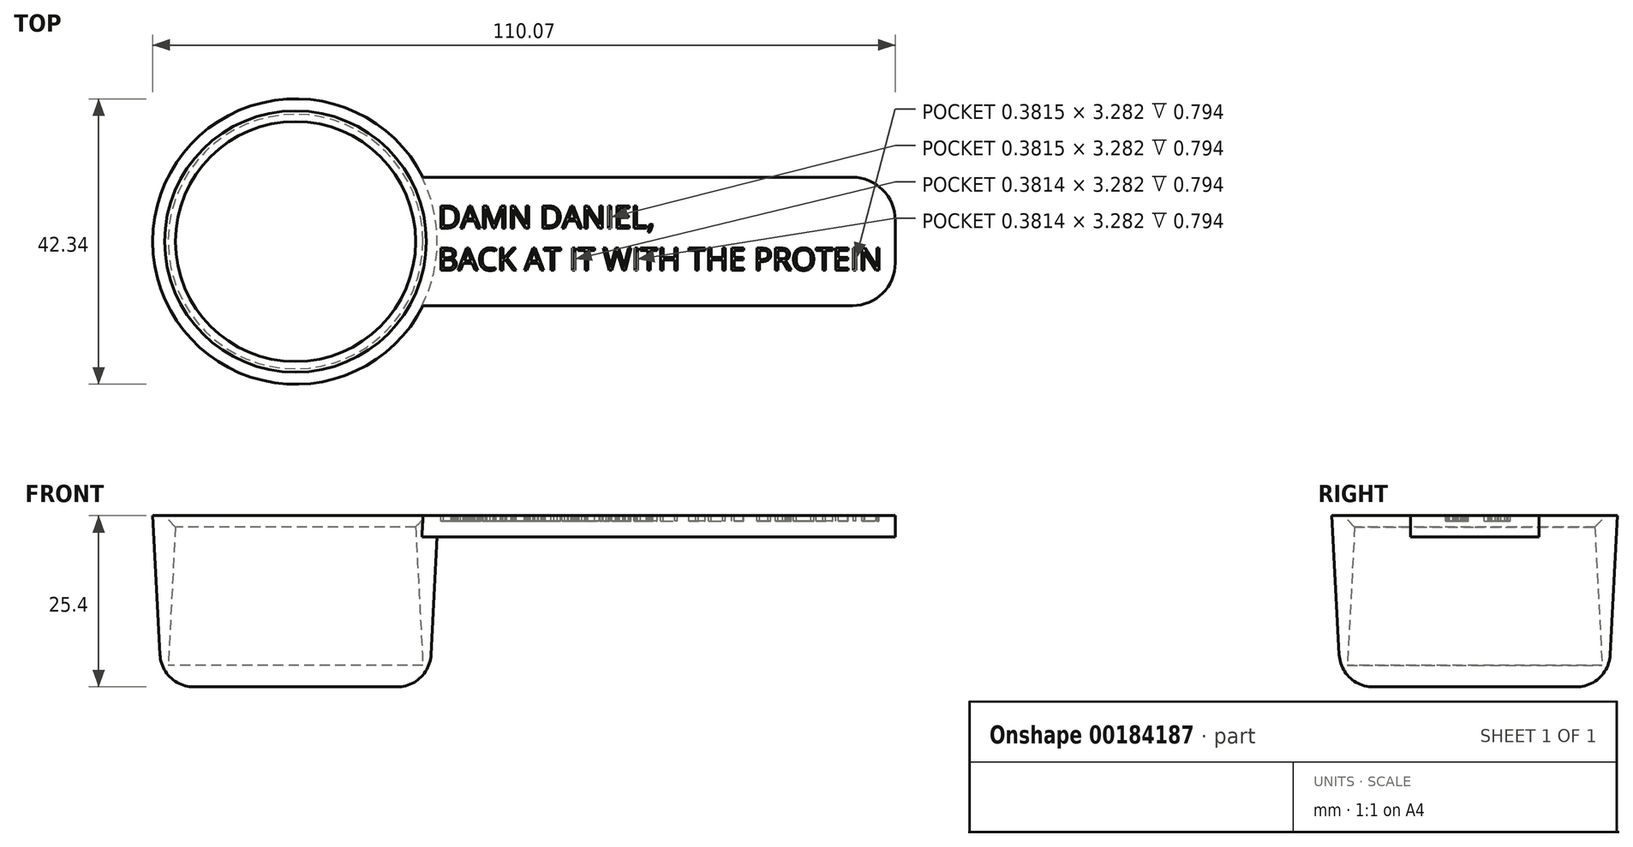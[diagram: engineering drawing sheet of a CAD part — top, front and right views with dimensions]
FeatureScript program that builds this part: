
annotation { "Feature Type Name" : "Feature", "Feature Type Description" : "" }
export const myFeature = defineFeature(function(context is Context, id is Id, definition is map)
    precondition{}
    {
        {
            var Q0;
            Q0=qCreatedBy(makeId("Top.planeOp"),FACE);
            var sketch = newSketch(context, id + "F0", { "sketchPlane" : qUnion([Q0])});
            skCircle(sketch, "E0", {"center": v(0, 0) * mm, "radius": 19.05 * mm});
            skCircle(sketch, "E1", {"center": v(0, 0) * mm, "radius": 19.84 * mm});
            skSolve(sketch);
        }
        {
            var Q0;
            Q0 = qSketchRegion(id + "F0", true);
            extrude(context, id + "F1", {"entities" : qUnion([Q0]), "depth" : 25.4 * mm, "hasDraft" : true, "draftAngle" : 3 * degree});
        }
        {
            var Q0;
            Q0=qCreatedBy(makeId("Top.planeOp"),FACE);
            var sketch = newSketch(context, id + "F2", { "sketchPlane" : qUnion([Q0])});
            skCircle(sketch, "E2", {"center": v(0, 0) * mm, "radius": 19.84 * mm});
            skSolve(sketch);
        }
        {
            var Q0;
            Q0 = qSketchRegion(id + "F2", true);
            extrude(context, id + "F3", {"entities" : qUnion([Q0]), "operationType" : NewBodyOperationType.ADD, "depth" : 3.17 * mm});
        }
        {
            var Q0;
            Q0=qCreatedBy(makeId("Right.planeOp"),FACE);
            cPlane(context, id + "F4", {"entities" : qUnion([Q0]), "cplaneType" : CPlaneType.OFFSET, "offset" : 88.9 * mm, "width" : 152.4 * mm, "height" : 152.4 * mm});
        }
        {
            var Q0;
            Q0=qCreatedBy(id+"F4.planeOp",FACE);
            var sketch = newSketch(context, id + "F5", { "sketchPlane" : qUnion([Q0])});
            skLineSegment(sketch, "E3", {"start": v(0, 0) * mm, "end": v(0, 25.4) * mm, "construction": true});
            skLineSegment(sketch, "E4", {"start": v(0, 25.4) * mm, "end": v(-9.53, 25.4) * mm});
            skLineSegment(sketch, "E5", {"start": v(-9.53, 25.4) * mm, "end": v(-9.53, 22.23) * mm});
            skLineSegment(sketch, "E6", {"start": v(-9.53, 22.23) * mm, "end": v(9.52, 22.23) * mm});
            skLineSegment(sketch, "E7", {"start": v(9.52, 22.23) * mm, "end": v(9.52, 25.4) * mm});
            skLineSegment(sketch, "E8", {"start": v(9.52, 25.4) * mm, "end": v(0, 25.4) * mm});
            skSolve(sketch);
        }
        {
            var Q0;
            Q0 = qSketchRegion(id + "F5", true);
            var Q1;
            Q1=makeQuery(id+"F1.opExtrude","SWEPT_FACE",FACE,{"disambiguationData":[OSD([sQuery(id+"F0.wireOp",EDGE,"E1")])]});
            extrude(context, id + "F6", {"entities" : qUnion([Q0]), "operationType" : NewBodyOperationType.ADD, "endBound" : BoundingType.UP_TO_SURFACE, "oppositeDirection" : true, "endBoundEntityFace" : qUnion([Q1]), "depth" : 25.4 * mm});
        }
        {
            var Q0;
            Q0=makeQuery(id+"F6.opExtrude","CAP_EDGE",EDGE,{"disambiguationData":[OSD([sQuery(id+"F5.wireOp",EDGE,"E5")])],"isStart":true});
            var Q1;
            Q1=makeQuery(id+"F6.opExtrude","CAP_EDGE",EDGE,{"disambiguationData":[OSD([sQuery(id+"F5.wireOp",EDGE,"E7")])],"isStart":true});
            fillet(context, id + "F7", {"entities" : qUnion([Q0, Q1]), "radius" : 6.35 * mm, "tangentPropagation" : true, "allowEdgeOverflow" : false});
        }
        {
            var Q0;
            Q0=makeQuery(id+"F6.boolean.opBoolean","MERGE",FACE,{"derivedFrom":[makeQuery(id+"F1.opExtrude","CAP_FACE",FACE,{"disambiguationData":[OSD([sQuery(id+"F0.wireOp",EDGE,"E0"),sQuery(id+"F0.wireOp",EDGE,"E1")])],"isStart":false}),makeQuery(id+"F6.opExtrude","SWEPT_FACE",FACE,{"disambiguationData":[OSD([sQuery(id+"F5.wireOp",EDGE,"E4"),sQuery(id+"F5.wireOp",EDGE,"E8")])]})]});
            var sketch = newSketch(context, id + "F8", { "sketchPlane" : qUnion([Q0])});
            skText(sketch, "E9", { "text": "DAMN DANIEL, \nBACK AT IT WITH THE PROTEIN", "fontName": "OpenSans-Regular.ttf"});
            const initialGuessF8  = {"E9": [0.02111, 0.00199, 1, 0, 0.00331]};
            skSetInitialGuess(sketch, initialGuessF8);
            skSolve(sketch);
        }
        {
            var Q0;
            Q0 = qSketchRegion(id + "F8", true);
            extrude(context, id + "F9", {"entities" : qUnion([Q0]), "operationType" : NewBodyOperationType.REMOVE, "oppositeDirection" : true, "depth" : 0.8 * mm});
        }
        {
            var Q0;
            Q0=makeQuery(id+"F1.opExtrude","CAP_EDGE",EDGE,{"disambiguationData":[OSD([sQuery(id+"F0.wireOp",EDGE,"E0")])],"isStart":false});
            chamfer(context, id + "F10", {"entities" : qUnion([Q0]), "width" : 1.59 * mm, "tangentPropagation" : true});
        }
        {
            var Q0;
            Q0=makeQuery(id+"F1.opExtrude","CAP_EDGE",EDGE,{"disambiguationData":[OSD([sQuery(id+"F0.wireOp",EDGE,"E1")])],"isStart":true});
            fillet(context, id + "F11", {"entities" : qUnion([Q0]), "radius" : 5.08 * mm, "tangentPropagation" : true, "allowEdgeOverflow" : false});
        }
    });
